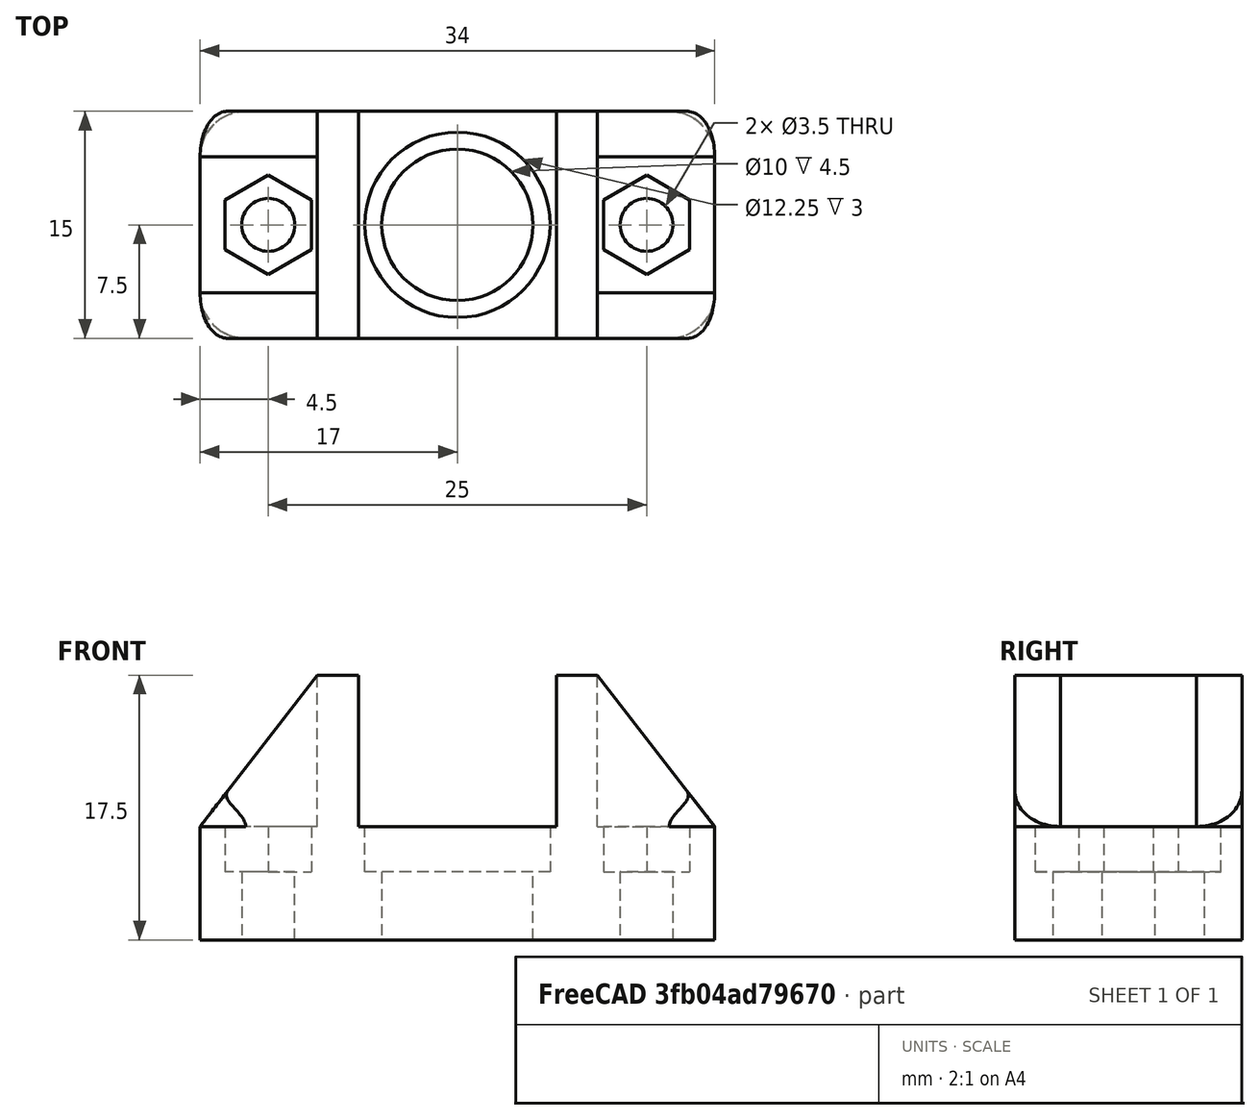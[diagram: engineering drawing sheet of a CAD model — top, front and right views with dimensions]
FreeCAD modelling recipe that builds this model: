
FCSTD DOCUMENT  (FreeCAD 0.21R33771 (Git))
Label: a2keyboardToPCT-db9
License: All rights reserved
LicenseURL: http://en.wikipedia.org/wiki/All_rights_reserved
objects: Sketcher::SketchObject×6, PartDesign::Fillet×4, PartDesign::Pad×3, PartDesign::Pocket×3, Mesh::Feature×1, PartDesign::Body×1
note: 27 computed .brp shape members not serialized (recipe doc carries the construction recipe); baked Part::Feature solids carry a one-line shape summary decoded from their .brp

FEATURE [Mesh::Feature] a2keyboardToPCT_enclosure  label="a2keyboardToPCT-enclosure"
FEATURE [Sketcher::SketchObject] Sketch
  FullyConstrained = true
  MapMode = 5
  Support = -> [XY_Plane]
  sketch-geometry (10):
    g0: Circle CenterX=0 CenterY=0 CenterZ=0 NormalX=0 NormalY=0 NormalZ=1 AngleXU=0 Radius=5
    g1: Circle CenterX=0 CenterY=0 CenterZ=0 NormalX=0 NormalY=0 NormalZ=1 AngleXU=0 Radius=6.125
    g2: LineSegment StartX=-6.55 StartY=7.5 StartZ=0 EndX=-6.55 EndY=-7.5 EndZ=0
    g3: Circle CenterX=-12.5 CenterY=0 CenterZ=0 NormalX=0 NormalY=0 NormalZ=1 AngleXU=0 Radius=1.75
    g4: Circle CenterX=12.5 CenterY=0 CenterZ=0 NormalX=0 NormalY=0 NormalZ=1 AngleXU=0 Radius=1.75
    g5: LineSegment StartX=-12.5 StartY=7.5 StartZ=0 EndX=-17 EndY=7.5 EndZ=0
    g6: LineSegment StartX=-17 StartY=7.5 StartZ=0 EndX=17 EndY=7.5 EndZ=0
    g7: LineSegment StartX=17 StartY=7.5 StartZ=0 EndX=17 EndY=-7.5 EndZ=0
    g8: LineSegment StartX=17 StartY=-7.5 StartZ=0 EndX=-17 EndY=-7.5 EndZ=0
    g9: LineSegment StartX=-17 StartY=-7.5 StartZ=0 EndX=-17 EndY=7.5 EndZ=0
  constraints (26):
    c: Coincident(g0,g-1)
    c: Coincident(g1,g0)
    c: Diameter(g0) = 10
    c: Diameter(g1) = 12.25
    c: DistanceX(g2,g0) = 6.55
    c: Symmetric(g2,g2,g-1)
    c: PointOnObject(g3,g-1)
    c: Diameter(g3) = 3.5
    c: DistanceX(g3,g0) = 12.5
    c: Equal(g4,g3)
    c: Symmetric(g3,g4,g-2)
    c: Horizontal(g5)
    c: DistanceY(g3,g5) = 7.5
    c: DistanceX(g5,g5) = 4.5
    c: Horizontal(g5,g2)
    c: Coincident(g6,g7)
    c: Coincident(g7,g8)
    c: Coincident(g8,g9)
    c: Coincident(g9,g6)
    c: Horizontal(g6)
    c: Vertical(g7)
    c: Vertical(g9)
    c: Coincident(g6,g5)
    c: PointOnObject(g2,g8)
    c: Symmetric(g8,g7,g-2)
    c: DistanceX(g8,g8) = 34
FEATURE [PartDesign::Pad] Pad
  Direction = (0,0,1)
  Length = 7.5
  Length2 = 10
  Profile = -> Sketch
  ReferenceAxis = -> Sketch [N_Axis]
  Type = 0
FEATURE [Sketcher::SketchObject] Sketch001
  FullyConstrained = true
  MapMode = 5
  Placement = pos=(0,0,7.5) rot=(0,0,1;0rad)
  Support = -> [Pad]
  sketch-geometry (1):
    g0: Circle CenterX=0 CenterY=0 CenterZ=0 NormalX=0 NormalY=0 NormalZ=1 AngleXU=0 Radius=6.125
  constraints (2):
    c: Coincident(g0,g-1)
    c: Diameter(g0) = 12.25
FEATURE [PartDesign::Pocket] Pocket
  BaseFeature = -> Pad
  Direction = (0,0,-1)
  Length = 3
  Length2 = 5
  Profile = -> Sketch001
  ReferenceAxis = -> Sketch001 [N_Axis]
  Type = 0
FEATURE [Sketcher::SketchObject] Sketch002
  ExternalGeometry = -> [Pocket]
  FullyConstrained = true
  MapMode = 5
  Placement = pos=(0,0,7.5) rot=(0,0,1;0rad)
  Support = -> [Pocket]
  sketch-geometry (15):
    g0: LineSegment StartX=-6.55 StartY=7.5 StartZ=0 EndX=-6.55 EndY=-7.5 EndZ=0
    g1: LineSegment StartX=6.55 StartY=7.5 StartZ=0 EndX=6.55 EndY=-7.5 EndZ=0
    g2: LineSegment StartX=-6.55 StartY=7.5 StartZ=0 EndX=-9.25 EndY=7.5 EndZ=0
    g3: LineSegment StartX=6.55 StartY=7.5 StartZ=0 EndX=9.25 EndY=7.5 EndZ=0
    g4: LineSegment StartX=-6.55 StartY=-7.5 StartZ=0 EndX=-9.25 EndY=-7.5 EndZ=0
    g5: LineSegment StartX=-9.25 StartY=7.5 StartZ=0 EndX=-9.25 EndY=-7.5 EndZ=0
    g6: LineSegment StartX=9.25 StartY=7.5 StartZ=0 EndX=9.25 EndY=-7.5 EndZ=0
    g7: LineSegment StartX=9.25 StartY=-7.5 StartZ=0 EndX=6.55 EndY=-7.5 EndZ=0
    g8: LineSegment StartX=-15.25 StartY=1.58771 StartZ=0 EndX=-15.25 EndY=-1.58771 EndZ=0
    g9: LineSegment StartX=-15.25 StartY=-1.58771 StartZ=0 EndX=-12.5 EndY=-3.17543 EndZ=0
    g10: LineSegment StartX=-12.5 StartY=-3.17543 StartZ=0 EndX=-9.75 EndY=-1.58771 EndZ=0
    g11: LineSegment StartX=-9.75 StartY=-1.58771 StartZ=0 EndX=-9.75 EndY=1.58771 EndZ=0
    g12: LineSegment StartX=-9.75 StartY=1.58771 StartZ=0 EndX=-12.5 EndY=3.17543 EndZ=0
    g13: LineSegment StartX=-12.5 StartY=3.17543 StartZ=0 EndX=-15.25 EndY=1.58771 EndZ=0
    g14: Circle CenterX=-12.5 CenterY=0 CenterZ=0 NormalX=0 NormalY=0 NormalZ=1 AngleXU=0 Radius=3.17543
  constraints (38):
    c: DistanceX(g0,g-1) = 6.55
    c: DistanceY(g-1,g0) = 7.5
    c: Symmetric(g0,g0,g-1)
    c: PointOnObject(g1,g-3)
    c: Vertical(g1)
    c: Symmetric(g1,g0,g-2)
    c: Coincident(g2,g0)
    c: PointOnObject(g2,g-3)
    c: Coincident(g3,g1)
    c: PointOnObject(g3,g-3)
    c: Equal(g3,g2)
    c: Coincident(g4,g0)
    c: Horizontal(g4)
    c: Coincident(g5,g2)
    c: Coincident(g5,g4)
    c: Vertical(g5)
    c: Coincident(g6,g3)
    c: Vertical(g6)
    c: Coincident(g7,g6)
    c: Coincident(g7,g1)
    c: Horizontal(g7)
    c: Coincident(g8,g9)
    c: Coincident(g9,g10)
    c: Coincident(g10,g11)
    c: Coincident(g11,g12)
    c: Coincident(g12,g13)
    c: Coincident(g13,g8)
    c: Equal(g8, g9-g13) x5
    c: PointOnObject(g8,g14)
    c: PointOnObject(g9,g14)
    c: PointOnObject(g10,g14)
    c: PointOnObject(g11,g14)
    c: PointOnObject(g12,g14)
    c: PointOnObject(g13,g14)
    c: Coincident(g14,g-4)
    c: Vertical(g8)
    c: DistanceX(g8,g10) = 5.5
    c: DistanceX(g10,g4) = 0.5
FEATURE [PartDesign::Pad] Pad001
  BaseFeature = -> Pocket
  Direction = (0,0,1)
  Length = 10
  Length2 = 10
  Profile = -> Sketch002
  ReferenceAxis = -> Sketch002 [N_Axis]
  Type = 0
FEATURE [Sketcher::SketchObject] Sketch003
  ExternalGeometry = -> [Pad001]
  FullyConstrained = true
  MapMode = 5
  Placement = pos=(0,0,7.5) rot=(0,0,1;0rad)
  Support = -> [Pad001]
  sketch-geometry (16):
    g0: LineSegment StartX=-9.25 StartY=4.5 StartZ=0 EndX=-17 EndY=4.5 EndZ=0
    g1: LineSegment StartX=-17 StartY=4.5 StartZ=0 EndX=-17 EndY=7.5 EndZ=0
    g2: LineSegment StartX=-17 StartY=7.5 StartZ=0 EndX=-9.25 EndY=7.5 EndZ=0
    g3: LineSegment StartX=-9.25 StartY=7.5 StartZ=0 EndX=-9.25 EndY=4.5 EndZ=0
    g4: LineSegment StartX=-9.25 StartY=-4.5 StartZ=0 EndX=-17 EndY=-4.5 EndZ=0
    g5: LineSegment StartX=-17 StartY=-4.5 StartZ=0 EndX=-17 EndY=-7.5 EndZ=0
    g6: LineSegment StartX=-17 StartY=-7.5 StartZ=0 EndX=-9.25 EndY=-7.5 EndZ=0
    g7: LineSegment StartX=-9.25 StartY=-7.5 StartZ=0 EndX=-9.25 EndY=-4.5 EndZ=0
    g8: LineSegment StartX=9.25 StartY=-4.5 StartZ=0 EndX=17 EndY=-4.5 EndZ=0
    g9: LineSegment StartX=17 StartY=-4.5 StartZ=0 EndX=17 EndY=-7.5 EndZ=0
    g10: LineSegment StartX=17 StartY=-7.5 StartZ=0 EndX=9.25 EndY=-7.5 EndZ=0
    g11: LineSegment StartX=9.25 StartY=-7.5 StartZ=0 EndX=9.25 EndY=-4.5 EndZ=0
    g12: LineSegment StartX=9.25 StartY=4.5 StartZ=0 EndX=17 EndY=4.5 EndZ=0
    g13: LineSegment StartX=17 StartY=4.5 StartZ=0 EndX=17 EndY=7.5 EndZ=0
    g14: LineSegment StartX=17 StartY=7.5 StartZ=0 EndX=9.25 EndY=7.5 EndZ=0
    g15: LineSegment StartX=9.25 StartY=7.5 StartZ=0 EndX=9.25 EndY=4.5 EndZ=0
  constraints (44):
    c: Coincident(g0,g1)
    c: Coincident(g1,g2)
    c: Coincident(g2,g3)
    c: Coincident(g3,g0)
    c: Horizontal(g0)
    c: Horizontal(g2)
    c: Vertical(g1)
    c: Vertical(g3)
    c: PointOnObject(g0,g-3)
    c: Coincident(g1,g-4)
    c: Coincident(g4,g5)
    c: Coincident(g5,g6)
    c: Coincident(g6,g7)
    c: Coincident(g7,g4)
    c: Horizontal(g4)
    c: Horizontal(g6)
    c: Vertical(g5)
    c: Vertical(g7)
    c: PointOnObject(g4,g-3)
    c: Coincident(g5,g-4)
    c: Coincident(g8,g9)
    c: Coincident(g9,g10)
    c: Coincident(g10,g11)
    c: Coincident(g11,g8)
    c: Horizontal(g8)
    c: Horizontal(g10)
    c: Vertical(g9)
    c: Vertical(g11)
    c: PointOnObject(g8,g-5)
    c: Coincident(g9,g-6)
    c: Coincident(g12,g13)
    c: Coincident(g13,g14)
    c: Coincident(g14,g15)
    c: Coincident(g15,g12)
    c: Horizontal(g12)
    c: Horizontal(g14)
    c: Vertical(g13)
    c: Vertical(g15)
    c: PointOnObject(g12,g-5)
    c: Coincident(g13,g-6)
    c: Equal(g13,g9)
    c: Equal(g9,g5)
    c: Equal(g5,g1)
    c: DistanceY(g5,g5) = 3
FEATURE [PartDesign::Pad] Pad002
  BaseFeature = -> Pad001
  Direction = (0,0,1)
  Length = 10
  Length2 = 10
  Profile = -> Sketch003
  ReferenceAxis = -> Sketch003 [N_Axis]
  Type = 0
FEATURE [Sketcher::SketchObject] Sketch004
  ExternalGeometry = -> [Pad002]
  FullyConstrained = true
  MapMode = 5
  Placement = pos=(0,7.5,0) rot=(0,0.707107,0.707107;3.14159rad)
  Support = -> [Pad002]
  sketch-geometry (6):
    g0: LineSegment StartX=-9.25 StartY=17.5 StartZ=0 EndX=-17 EndY=7.5 EndZ=0
    g1: LineSegment StartX=9.25 StartY=17.5 StartZ=0 EndX=17 EndY=7.5 EndZ=0
    g2: LineSegment StartX=17 StartY=7.5 StartZ=0 EndX=17 EndY=17.5 EndZ=0
    g3: LineSegment StartX=17 StartY=17.5 StartZ=0 EndX=9.25 EndY=17.5 EndZ=0
    g4: LineSegment StartX=-9.25 StartY=17.5 StartZ=0 EndX=-17 EndY=17.5 EndZ=0
    g5: LineSegment StartX=-17 StartY=17.5 StartZ=0 EndX=-17 EndY=7.5 EndZ=0
  constraints (12):
    c: Coincident(g0,g-3)
    c: Coincident(g0,g-4)
    c: Coincident(g1,g-5)
    c: Coincident(g1,g-6)
    c: Coincident(g2,g1)
    c: Coincident(g2,g-5)
    c: Coincident(g3,g2)
    c: Coincident(g3,g1)
    c: Coincident(g4,g0)
    c: Coincident(g4,g-3)
    c: Coincident(g5,g4)
    c: Coincident(g5,g0)
FEATURE [PartDesign::Pocket] Pocket001
  BaseFeature = -> Pad002
  Direction = (0,-1,2e-16)
  Length = 5
  Length2 = 5
  Profile = -> Sketch004
  ReferenceAxis = -> Sketch004 [N_Axis]
  Type = 1
FEATURE [PartDesign::Fillet] Fillet
  Base = -> Pocket001 [Edge2]
  BaseFeature = -> Pocket001
  Radius = 3
  SupportTransform = false
  UseAllEdges = false
FEATURE [PartDesign::Fillet] Fillet001
  Base = -> Fillet [Edge37]
  BaseFeature = -> Fillet
  Radius = 3
  SupportTransform = false
  UseAllEdges = false
FEATURE [PartDesign::Fillet] Fillet002
  Base = -> Fillet001 [Edge15]
  BaseFeature = -> Fillet001
  Radius = 3
  SupportTransform = false
  UseAllEdges = false
FEATURE [PartDesign::Fillet] Fillet003
  Base = -> Fillet002 [Edge24]
  BaseFeature = -> Fillet002
  Radius = 3
  SupportTransform = false
  UseAllEdges = false
FEATURE [Sketcher::SketchObject] Sketch005
  ExternalGeometry = -> [Fillet003]
  FullyConstrained = true
  MapMode = 5
  Placement = pos=(0,0,7.5) rot=(0,0,1;0rad)
  Support = -> [Fillet003]
  sketch-geometry (14):
    g0: LineSegment StartX=-12.5 StartY=3.2909 StartZ=0 EndX=-15.35 EndY=1.64545 EndZ=0
    g1: LineSegment StartX=-15.35 StartY=1.64545 StartZ=0 EndX=-15.35 EndY=-1.64545 EndZ=0
    g2: LineSegment StartX=-15.35 StartY=-1.64545 StartZ=0 EndX=-12.5 EndY=-3.2909 EndZ=0
    g3: LineSegment StartX=-12.5 StartY=-3.2909 StartZ=0 EndX=-9.65 EndY=-1.64545 EndZ=0
    g4: LineSegment StartX=-9.65 StartY=-1.64545 StartZ=0 EndX=-9.65 EndY=1.64545 EndZ=0
    g5: LineSegment StartX=-9.65 StartY=1.64545 StartZ=0 EndX=-12.5 EndY=3.2909 EndZ=0
    g6: Circle CenterX=-12.5 CenterY=0 CenterZ=0 NormalX=0 NormalY=0 NormalZ=1 AngleXU=0 Radius=3.2909
    g7: LineSegment StartX=9.65 StartY=1.64545 StartZ=0 EndX=9.65 EndY=-1.64545 EndZ=0
    g8: LineSegment StartX=9.65 StartY=-1.64545 StartZ=0 EndX=12.5 EndY=-3.2909 EndZ=0
    g9: LineSegment StartX=12.5 StartY=-3.2909 StartZ=0 EndX=15.35 EndY=-1.64545 EndZ=0
    g10: LineSegment StartX=15.35 StartY=-1.64545 StartZ=0 EndX=15.35 EndY=1.64545 EndZ=0
    g11: LineSegment StartX=15.35 StartY=1.64545 StartZ=0 EndX=12.5 EndY=3.2909 EndZ=0
    g12: LineSegment StartX=12.5 StartY=3.2909 StartZ=0 EndX=9.65 EndY=1.64545 EndZ=0
    g13: Circle CenterX=12.5 CenterY=0 CenterZ=0 NormalX=0 NormalY=0 NormalZ=1 AngleXU=0 Radius=3.2909
  constraints (32):
    c: Coincident(g0,g1)
    c: Coincident(g1,g2)
    c: Coincident(g2,g3)
    c: Coincident(g3,g4)
    c: Coincident(g4,g5)
    c: Coincident(g5,g0)
    c: Equal(g0, g1-g5) x5
    c: PointOnObject(g0,g6)
    c: PointOnObject(g1,g6)
    c: PointOnObject(g2,g6)
    c: PointOnObject(g3,g6)
    c: PointOnObject(g4,g6)
    c: PointOnObject(g5,g6)
    c: Coincident(g6,g-3)
    c: Vertical(g1)
    c: DistanceX(g1,g3) = 5.7
    c: Coincident(g7,g8)
    c: Coincident(g8,g9)
    c: Coincident(g9,g10)
    c: Coincident(g10,g11)
    c: Coincident(g11,g12)
    c: Coincident(g12,g7)
    c: Equal(g7, g8-g12) x5
    c: PointOnObject(g7,g13)
    c: PointOnObject(g8,g13)
    c: PointOnObject(g9,g13)
    c: PointOnObject(g10,g13)
    c: PointOnObject(g11,g13)
    c: PointOnObject(g12,g13)
    c: Vertical(g7)
    c: Equal(g4,g7)
    c: Symmetric(g6,g13,g-2)
FEATURE [PartDesign::Pocket] Pocket002
  BaseFeature = -> Fillet003
  Direction = (0,0,-1)
  Length = 3
  Length2 = 5
  Profile = -> Sketch005
  ReferenceAxis = -> Sketch005 [N_Axis]
  Type = 0
FEATURE [PartDesign::Body] Body
  Group = -> [Sketch,Pad,Sketch001,Pocket,Sketch002,Pad001,Sketch003,Pad002,Sketch004,Pocket001,Fillet,Fillet001,Fillet002,Fillet003,Sketch005,Pocket002]
  Origin = -> Origin
  Tip = -> Pocket002
